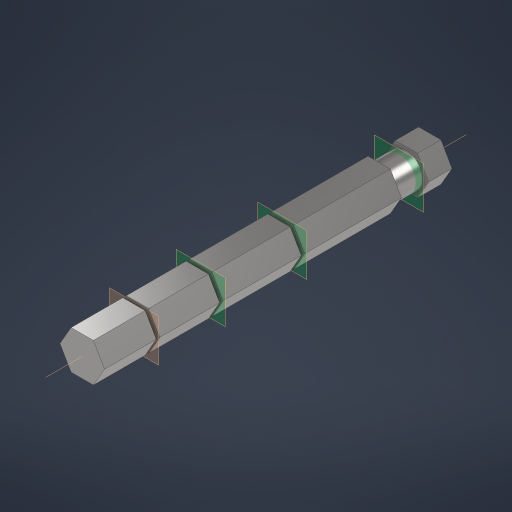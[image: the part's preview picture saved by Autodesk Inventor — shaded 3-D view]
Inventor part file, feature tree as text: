
AUTODESK INVENTOR PART (.ipt)
format: ipt  version: 2024 (Build 280153000, 153)  size: 256,512 bytes
history: native  units: in
note: dims shown in document units (in); Inventor stores cm internally (conversion verified against a paired STEP export)
features: sketch x7, extrude x5, plane x4, other x1, hole x1, projected_geometry x1
ambient origin geometry x8: Origin, YZ Plane, XZ Plane, XY Plane, X Axis, Y Axis, Z Axis, Center Point
bodies: Solid1 (feature_tree)
feature tree (19):
  extrude  "Extrusion1"  Depth=4.5in TaperAngle=0.0deg
  other  "Work Axis1"
  hole  "Hole3"  [1 undecoded]
  plane  "Work Plane4"
  plane  "Work Plane5"
  plane  "Work Plane6"
  plane  "Work Plane7"
  sketch  "Sketch16"  dims[d60=0.392in d62=0.0in d63=0.042in d64=0.4375in]
  extrude  "Extrusion10"  [1 undecoded]
  sketch  "Sketch1"  dims[d0=0.5in d1=4.5in d2=0.0in]
  sketch  "Sketch10"  dims[d33=0.156in d34=0.5in d35=0.375in d36=0.25in d37=0.5635in d38=0.536in d39=0.8108in d40=-0.4in]
  sketch  "Sketch17"  dims[d65=0.092in d66=0.255in d67=0.0in d68=0.0in d69=0.392in d71=0.0in d72=0.042in]
  projected_geometry  "Projected Loop1"
  sketch  "Sketch13"  dims[d45=-1.91in d50=-2.968in]
  sketch  "Sketch15"  dims[d51=0.392in d53=0.0in d54=0.042in d55=-0.67in]
  sketch  "Sketch18"
  extrude  "Extrusion7"  [1 undecoded]
  extrude  "Extrusion9"  Depth=0.042in
  extrude  "Extrusion11"  Depth=0.042in TaperAngle=0.0deg
note: 3 required parameter values undecoded (feature->parameter linkage not recoverable at this tier; creation-order binding heuristic only, values carry confidence <= 0.55)
